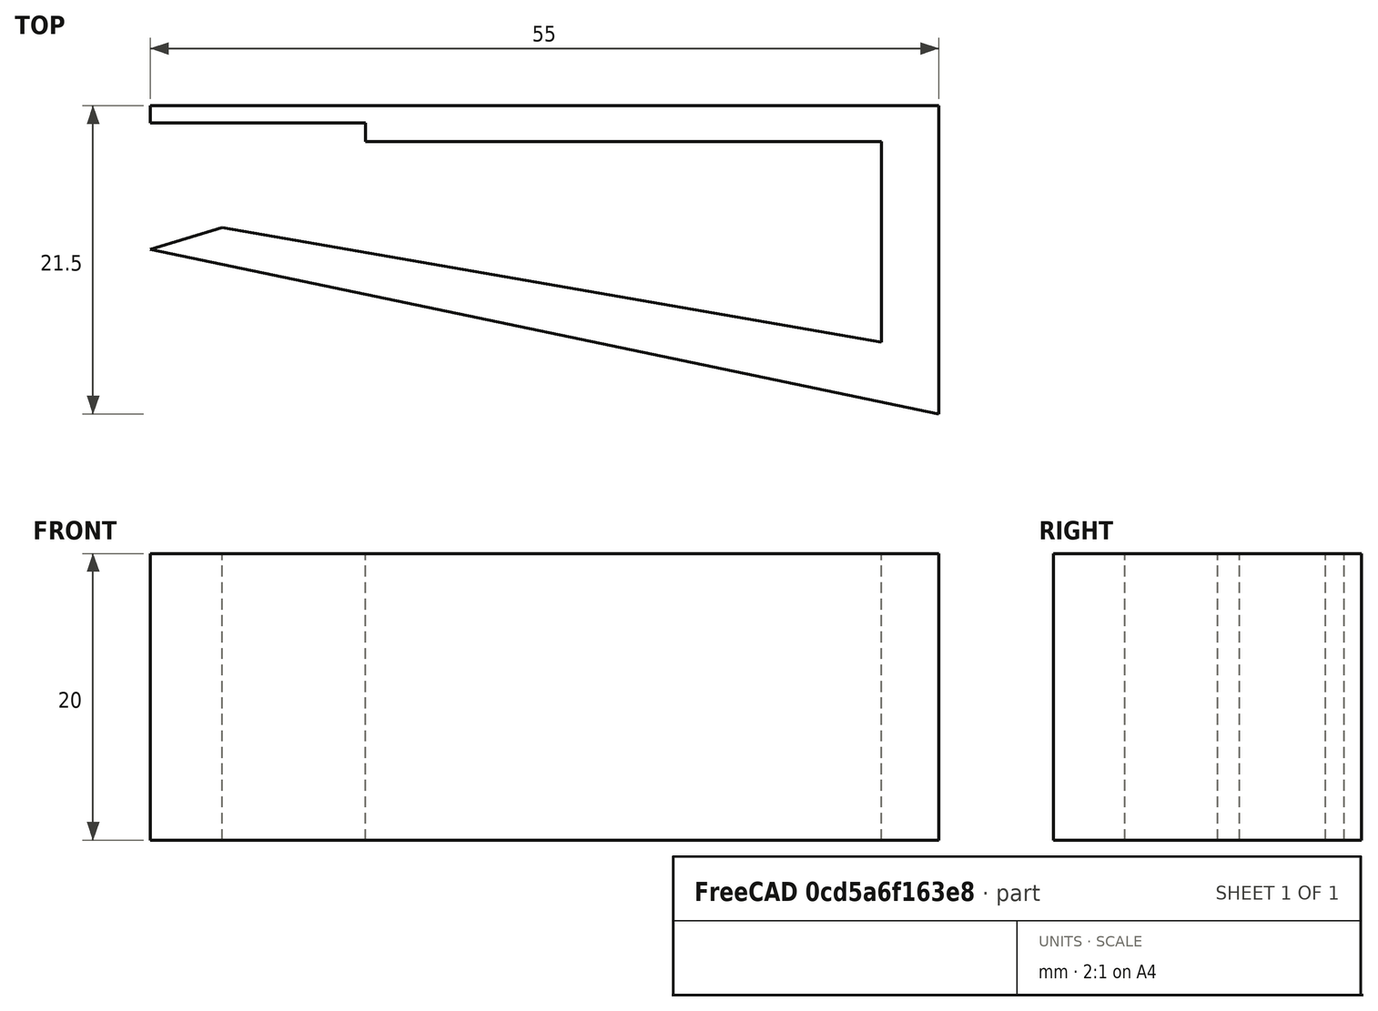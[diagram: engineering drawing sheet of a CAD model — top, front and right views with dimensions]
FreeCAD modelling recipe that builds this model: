
FCSTD DOCUMENT  (FreeCAD 0.15R4671 (Git))
Label: heaterBracketHigh
License: CC-BY 3.0
LicenseURL: http://creativecommons.org/licenses/by/3.0/
objects: Sketcher::SketchObject×1, PartDesign::Pad×1
note: 3 computed .brp shape members not serialized (recipe doc carries the construction recipe); baked Part::Feature solids carry a one-line shape summary decoded from their .brp

FEATURE [Sketcher::SketchObject] Sketch  label="Profil"
  sketch-geometry (11):
    g0: LineSegment StartX=0 StartY=71 StartZ=0 EndX=-7 EndY=71 EndZ=0
    g1: LineSegment StartX=-40 StartY=22.5 StartZ=0 EndX=-4 EndY=22.5 EndZ=0
    g2: LineSegment StartX=-4 StartY=22.5 StartZ=0 EndX=-4 EndY=8.5 EndZ=0
    g3: LineSegment StartX=-4 StartY=8.5 StartZ=0 EndX=-50 EndY=16.5 EndZ=0
    g4: LineSegment StartX=-50 StartY=16.5 StartZ=0 EndX=-55 EndY=14.9898 EndZ=0
    g5: LineSegment StartX=-55 StartY=14.9898 StartZ=0 EndX=0 EndY=3.5 EndZ=0
    g6: LineSegment StartX=0 StartY=25 StartZ=0 EndX=-55 EndY=25 EndZ=0
    g7: LineSegment StartX=0 StartY=25 StartZ=0 EndX=0 EndY=3.5 EndZ=0
    g8: LineSegment StartX=-55 StartY=25 StartZ=0 EndX=-55 EndY=23.8 EndZ=0
    g9: LineSegment StartX=-55 StartY=23.8 StartZ=0 EndX=-40 EndY=23.8 EndZ=0
    g10: LineSegment StartX=-40 StartY=23.8 StartZ=0 EndX=-40 EndY=22.5 EndZ=0
  constraints (29):
    c: Horizontal(g0)
    c: DistanceX(g0) = -7
    c: Horizontal(g1)
    c: Vertical(g2)
    c: Coincident(g2,g3)
    c: Coincident(g3,g4)
    c: Coincident(g4,g5)
    c: Coincident(g1,g2)
    c: DistanceY(g1,g2) = -14
    c: DistanceY(g2,g5) = -5
    c: DistanceY(g3,g1) = 6
    c: DistanceY(g6,g1) = -2.5
    c: Horizontal(g6)
    c: DistanceX(g-1,g2) = -4
    c: Coincident(g6,g7)
    c: Coincident(g5,g7)
    c: DistanceX(g-1,g6) = -55
    c: DistanceY(g-1,g6) = 25
    c: DistanceX(g-1,g3) = -50
    c: DistanceX(g4,g3) = 5
    c: DistanceX(g6,g1) = 15
    c: Coincident(g8,g9)
    c: Coincident(g9,g10)
    c: Coincident(g1,g10)
    c: Coincident(g6,g8)
    c: Vertical(g8)
    c: Vertical(g10)
    c: DistanceY(g10) = -1.3
    c: Horizontal(g9)
FEATURE [PartDesign::Pad] Pad  label="Corps"
  Length = 20
  Length2 = 100
  Sketch = -> Sketch
  Type = 0
